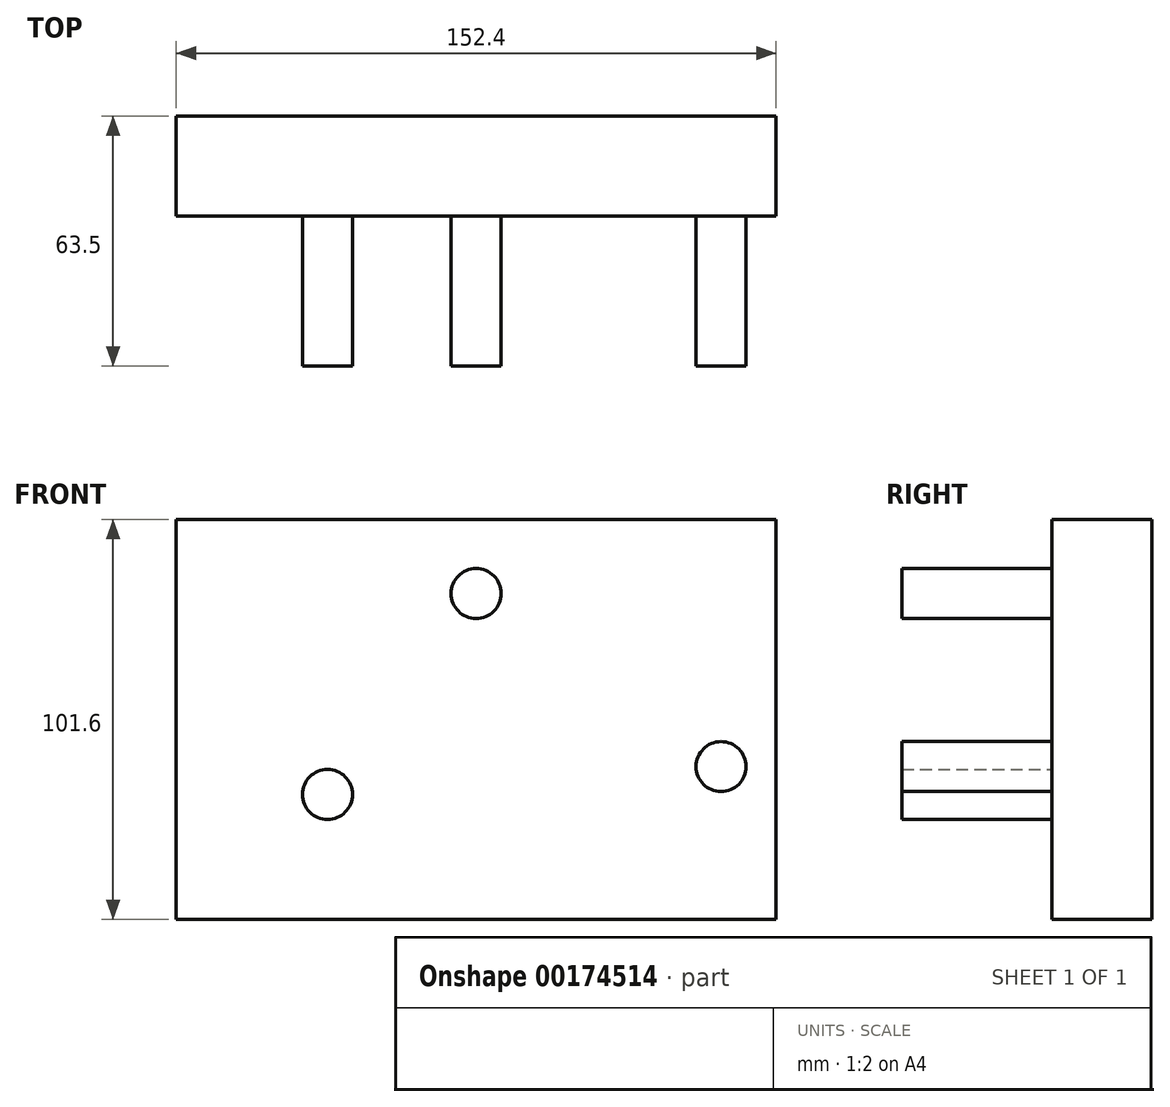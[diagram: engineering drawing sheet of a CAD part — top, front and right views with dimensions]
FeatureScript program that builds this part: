
annotation { "Feature Type Name" : "Feature", "Feature Type Description" : "" }
export const myFeature = defineFeature(function(context is Context, id is Id, definition is map)
    precondition{}
    {
        {
            var Q0;
            Q0=qCreatedBy(makeId("Front.planeOp"),FACE);
            var sketch = newSketch(context, id + "F0", { "sketchPlane" : qUnion([Q0])});
            skLineSegment(sketch, "E0.bottom", {"start": v(-76.2, 50.8) * mm, "end": v(76.2, 50.8) * mm});
            skLineSegment(sketch, "E0.top", {"start": v(-76.2, -50.8) * mm, "end": v(76.2, -50.8) * mm});
            skLineSegment(sketch, "E0.left", {"start": v(-76.2, 50.8) * mm, "end": v(-76.2, -50.8) * mm});
            skLineSegment(sketch, "E0.right", {"start": v(76.2, 50.8) * mm, "end": v(76.2, -50.8) * mm});
            skSolve(sketch);
        }
        {
            var Q0;
            Q0=makeQuery(id+"F0.imprint","IMPRINT",FACE,{"disambiguationData":[TD([[makeQuery(id+"F0.imprint","IMPRINT",EDGE,{"derivedFrom":sQuery(id+"F0.wireOp",EDGE,"E0.bottom")}),-1.0]])]});
            extrude(context, id + "F1", {"entities" : qUnion([Q0]), "depth" : 25.4 * mm});
        }
        {
            var Q0;
            Q0=makeQuery(id+"F1.opExtrude","CAP_FACE",FACE,{"disambiguationData":[OSD([sQuery(id+"F0.wireOp",EDGE,"E0.bottom"),sQuery(id+"F0.wireOp",EDGE,"E0.top"),sQuery(id+"F0.wireOp",EDGE,"E0.left"),sQuery(id+"F0.wireOp",EDGE,"E0.right")])],"isStart":false});
            var sketch = newSketch(context, id + "F2", { "sketchPlane" : qUnion([Q0])});
            skCircle(sketch, "E1", {"center": v(0, 32) * mm, "radius": 6.35 * mm});
            skCircle(sketch, "E2", {"center": v(-37.77, -19.05) * mm, "radius": 6.35 * mm});
            skCircle(sketch, "E3", {"center": v(62.23, -11.98) * mm, "radius": 6.35 * mm});
            skSolve(sketch);
        }
        {
            var Q0;
            Q0=makeQuery(id+"F2.imprint","IMPRINT",FACE,{"disambiguationData":[TD([[makeQuery(id+"F2.imprint","IMPRINT",EDGE,{"derivedFrom":sQuery(id+"F2.wireOp",EDGE,"E2")}),1.0]])]});
            var Q1;
            Q1=makeQuery(id+"F2.imprint","IMPRINT",FACE,{"disambiguationData":[TD([[makeQuery(id+"F2.imprint","IMPRINT",EDGE,{"derivedFrom":sQuery(id+"F2.wireOp",EDGE,"E1")}),1.0]])]});
            var Q2;
            Q2=makeQuery(id+"F2.imprint","IMPRINT",FACE,{"disambiguationData":[TD([[makeQuery(id+"F2.imprint","IMPRINT",EDGE,{"derivedFrom":sQuery(id+"F2.wireOp",EDGE,"E3")}),1.0]])]});
            extrude(context, id + "F3", {"entities" : qUnion([Q0, Q1, Q2]), "operationType" : NewBodyOperationType.ADD, "depth" : 38.1 * mm});
        }
    });
